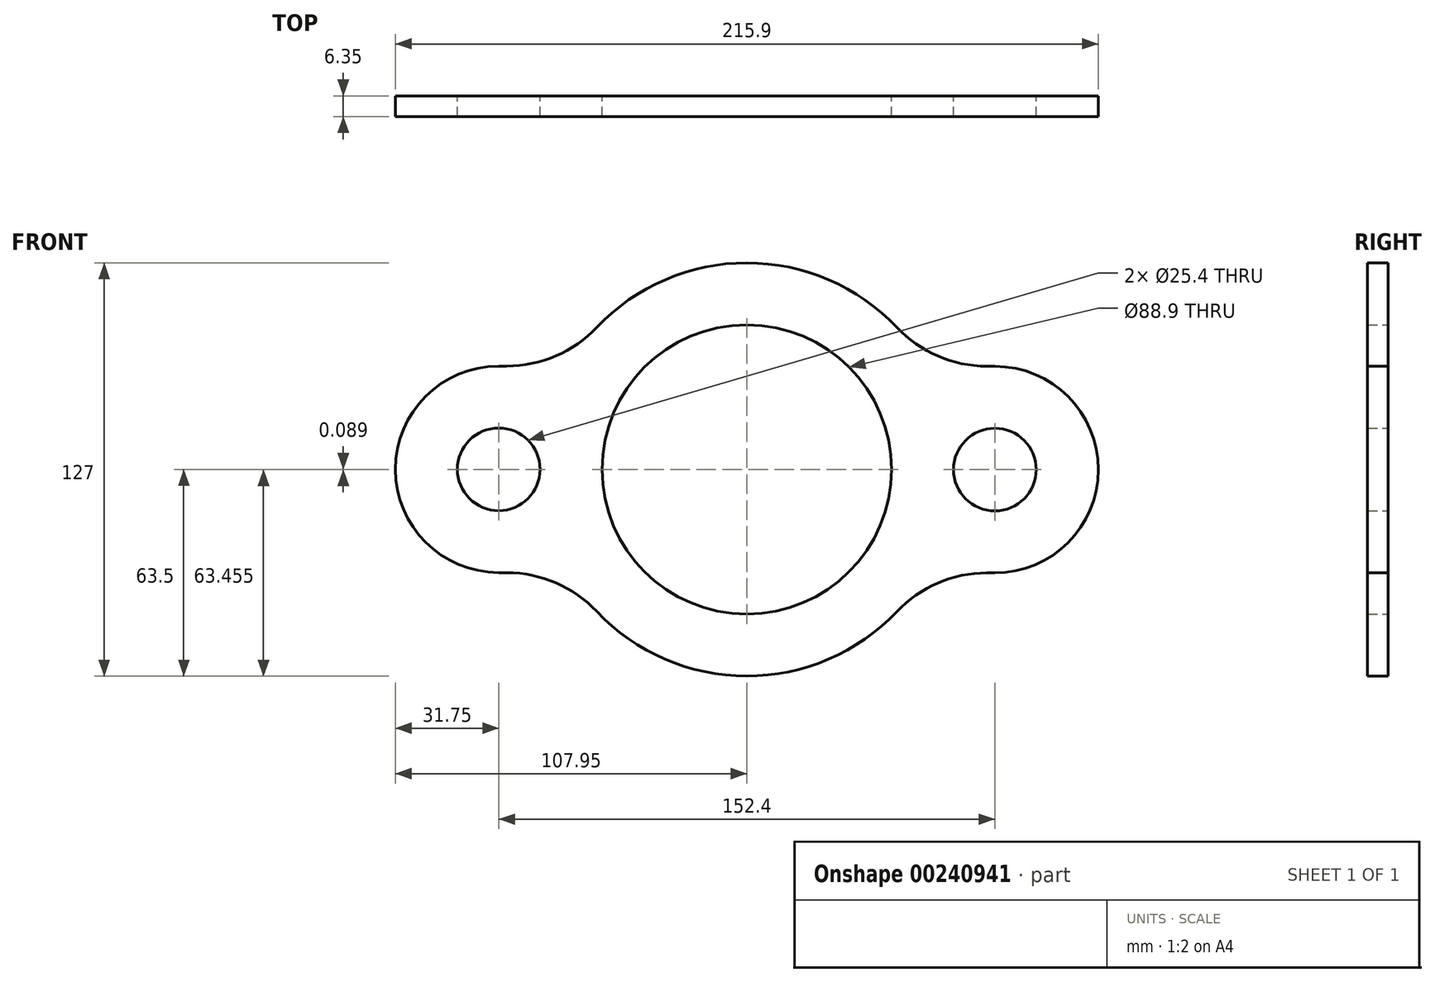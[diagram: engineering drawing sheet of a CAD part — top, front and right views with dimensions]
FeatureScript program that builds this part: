
annotation { "Feature Type Name" : "Feature", "Feature Type Description" : "" }
export const myFeature = defineFeature(function(context is Context, id is Id, definition is map)
    precondition{}
    {
        {
            var Q0;
            Q0=qCreatedBy(makeId("Front.planeOp"),FACE);
            var sketch = newSketch(context, id + "F0", { "sketchPlane" : qUnion([Q0])});
            skCircle(sketch, "E0", {"center": v(0, 0) * mm, "radius": 44.45 * mm});
            skCircle(sketch, "E1", {"center": v(-76.2, 0.04) * mm, "radius": 12.7 * mm});
            skCircle(sketch, "E2", {"center": v(76.2, -0.04) * mm, "radius": 12.7 * mm});
            skArc(sketch, "E3", {"start": v(76.2, 31.7) * mm, "mid": v(107.95, -0.04) * mm, "end": v(76.2, -31.8) * mm});
            skArc(sketch, "E4", {"start": v(-76.2, 31.8) * mm, "mid": v(-107.95, 0.04) * mm, "end": v(-76.2, -31.7) * mm});
            skArc(sketch, "E5", {"start": v(46.09, -43.68) * mm, "mid": v(-0.03, -63.5) * mm, "end": v(-46.13, -43.63) * mm});
            skArc(sketch, "E6", {"start": v(-46.09, 43.68) * mm, "mid": v(0.03, 63.5) * mm, "end": v(46.13, 43.63) * mm});
            skLineSegment(sketch, "E7", {"start": v(-76.2, 31.8) * mm, "end": v(-73.74, 31.8) * mm});
            skLineSegment(sketch, "E8", {"start": v(76.2, 31.7) * mm, "end": v(73.65, 31.72) * mm});
            skLineSegment(sketch, "E9", {"start": v(76.2, -31.8) * mm, "end": v(73.74, -31.8) * mm});
            skLineSegment(sketch, "E10", {"start": v(-73.65, -31.72) * mm, "end": v(-76.2, -31.7) * mm});
            skPoint(sketch, "E11.visualSharp", {"position": v(-54.97, 31.8) * mm});
            skArc(sketch, "E11.filletArc", {"start": v(-73.74, 31.8) * mm, "mid": v(-58.69, 34.9) * mm, "end": v(-46.09, 43.68) * mm});
            skPoint(sketch, "E12.visualSharp", {"position": v(-54.97, -31.8) * mm});
            skArc(sketch, "E12.filletArc", {"start": v(-46.13, -43.63) * mm, "mid": v(-58.67, -34.85) * mm, "end": v(-73.65, -31.72) * mm});
            skPoint(sketch, "E13.visualSharp", {"position": v(54.97, -31.8) * mm});
            skArc(sketch, "E13.filletArc", {"start": v(73.74, -31.8) * mm, "mid": v(58.69, -34.9) * mm, "end": v(46.09, -43.68) * mm});
            skPoint(sketch, "E14.visualSharp", {"position": v(54.97, 31.8) * mm});
            skArc(sketch, "E14.filletArc", {"start": v(46.13, 43.63) * mm, "mid": v(58.67, 34.85) * mm, "end": v(73.65, 31.72) * mm});
            skLineSegment(sketch, "E15", {"start": v(0, 0) * mm, "end": v(29.29, -56.34) * mm});
            skSolve(sketch);
        }
        {
            var Q0;
            Q0=makeQuery(id+"F0.imprint","IMPRINT",FACE,{"disambiguationData":[TD([[makeQuery(id+"F0.imprint","IMPRINT",EDGE,{"derivedFrom":sQuery(id+"F0.wireOp",EDGE,"E0")}),-1.0]])]});
            extrude(context, id + "F1", {"entities" : qUnion([Q0]), "depth" : 6.35 * mm});
        }
    });
